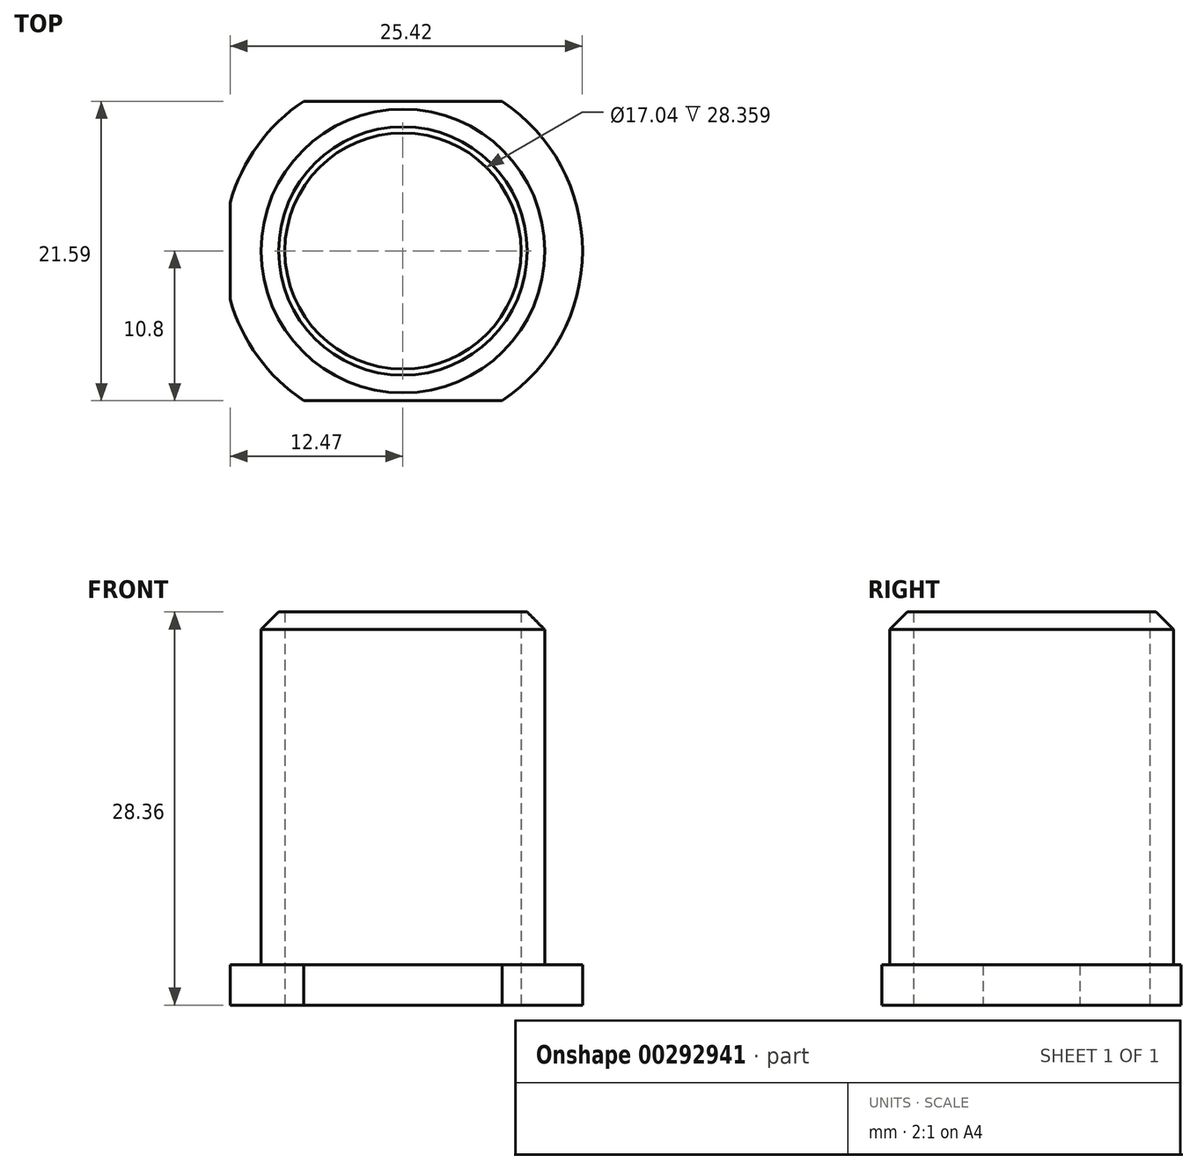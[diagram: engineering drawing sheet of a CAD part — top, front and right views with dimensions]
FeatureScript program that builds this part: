
annotation { "Feature Type Name" : "Feature", "Feature Type Description" : "" }
export const myFeature = defineFeature(function(context is Context, id is Id, definition is map)
    precondition{}
    {
        {
            var Q0;
            Q0=qCreatedBy(makeId("Top.planeOp"),FACE);
            var sketch = newSketch(context, id + "F0", { "sketchPlane" : qUnion([Q0])});
            skCircle(sketch, "E0", {"center": v(0, 0) * mm, "radius": 10.24 * mm});
            skCircle(sketch, "E1", {"center": v(0, 0) * mm, "radius": 8.51 * mm});
            skSolve(sketch);
        }
        {
            var Q0;
            Q0=makeQuery(id+"F0.imprint","IMPRINT",FACE,{"disambiguationData":[TD([[makeQuery(id+"F0.imprint","IMPRINT",EDGE,{"derivedFrom":sQuery(id+"F0.wireOp",EDGE,"E0")}),1.0]])]});
            extrude(context, id + "F1", {"entities" : qUnion([Q0]), "depth" : 28.36 * mm});
        }
        {
            var Q0;
            Q0=qCreatedBy(makeId("Top.planeOp"),FACE);
            var sketch = newSketch(context, id + "F2", { "sketchPlane" : qUnion([Q0])});
            skLineSegment(sketch, "E2.bottom", {"start": v(7.16, -10.8) * mm, "end": v(-7.16, -10.8) * mm});
            skLineSegment(sketch, "E2.top", {"start": v(7.16, 10.8) * mm, "end": v(-7.16, 10.8) * mm});
            skLineSegment(sketch, "E2.right", {"start": v(-12.47, -3.5) * mm, "end": v(-12.47, 3.5) * mm});
            skPoint(sketch, "E2.middle", {"position": v(0, 0) * mm});
            skArc(sketch, "E3", {"start": v(7.16, -10.8) * mm, "mid": v(12.95, 0) * mm, "end": v(7.16, 10.8) * mm});
            skPoint(sketch, "E4.orphan", {"position": v(-12.47, 10.8) * mm});
            skPoint(sketch, "E5.orphan", {"position": v(-12.47, -10.8) * mm});
            skArc(sketch, "E6.trimOffspring", {"start": v(-7.16, 10.8) * mm, "mid": v(-10.47, 7.63) * mm, "end": v(-12.47, 3.5) * mm});
            skArc(sketch, "E7.trimOffspring", {"start": v(-12.47, -3.5) * mm, "mid": v(-10.47, -7.63) * mm, "end": v(-7.16, -10.8) * mm});
            skPoint(sketch, "E8.orphan", {"position": v(12.47, 10.8) * mm});
            skPoint(sketch, "E9.orphan", {"position": v(12.47, -10.8) * mm});
            skSolve(sketch);
        }
        {
            var Q0;
            Q0=makeQuery(id+"F2.imprint","IMPRINT",FACE,{"disambiguationData":[TD([[makeQuery(id+"F2.imprint","IMPRINT",EDGE,{"derivedFrom":sQuery(id+"F2.wireOp",EDGE,"E2.bottom")}),-1.0]])]});
            extrude(context, id + "F3", {"entities" : qUnion([Q0]), "operationType" : NewBodyOperationType.ADD, "depth" : 2.9 * mm});
        }
        {
            var Q0;
            Q0=makeQuery(id+"F3.boolean.opBoolean","MERGE",FACE,{"derivedFrom":[makeQuery(id+"F1.opExtrude","CAP_FACE",FACE,{"disambiguationData":[OSD([sQuery(id+"F0.wireOp",EDGE,"E0"),sQuery(id+"F0.wireOp",EDGE,"E1")])],"isStart":true}),makeQuery(id+"F3.opExtrude","CAP_FACE",FACE,{"disambiguationData":[OSD([sQuery(id+"F2.wireOp",EDGE,"E2.bottom"),sQuery(id+"F2.wireOp",EDGE,"E2.top"),sQuery(id+"F2.wireOp",EDGE,"E2.right"),sQuery(id+"F2.wireOp",EDGE,"E3"),sQuery(id+"F2.wireOp",EDGE,"E6.trimOffspring"),sQuery(id+"F2.wireOp",EDGE,"E7.trimOffspring")])],"isStart":true})]});
            var sketch = newSketch(context, id + "F4", { "sketchPlane" : qUnion([Q0])});
            skCircle(sketch, "E10", {"center": v(0, 0) * mm, "radius": 8.52 * mm});
            skSolve(sketch);
        }
        {
            var Q0;
            Q0=sQuery(id+"F4.wireOp",VERTEX,"E10.center");
            var Q1;
            Q1=makeQuery(id+"F1.opExtrude","SWEPT_BODY",BODY,{"disambiguationData":[OSD([sQuery(id+"F0.wireOp",EDGE,"E0"),sQuery(id+"F0.wireOp",EDGE,"E1")])]});
            hole(context, id + "F5", {"style" : HoleStyle.SIMPLE, "endStyle" : HoleEndStyle.THROUGH, "holeDiameter" : 17.04 * mm, "tappedDepth" : 12.7 * mm, "tapClearance" : 3, "startFromSketch" : true, "locations" : qUnion([Q0]), "scope" : qUnion([Q1])});
        }
        {
            var Q0;
            Q0=makeQuery(id+"F1.opExtrude","CAP_EDGE",EDGE,{"disambiguationData":[OSD([sQuery(id+"F0.wireOp",EDGE,"E0")])],"isStart":false});
            chamfer(context, id + "F6", {"entities" : qUnion([Q0]), "width" : 1.27 * mm, "tangentPropagation" : true});
        }
    });
